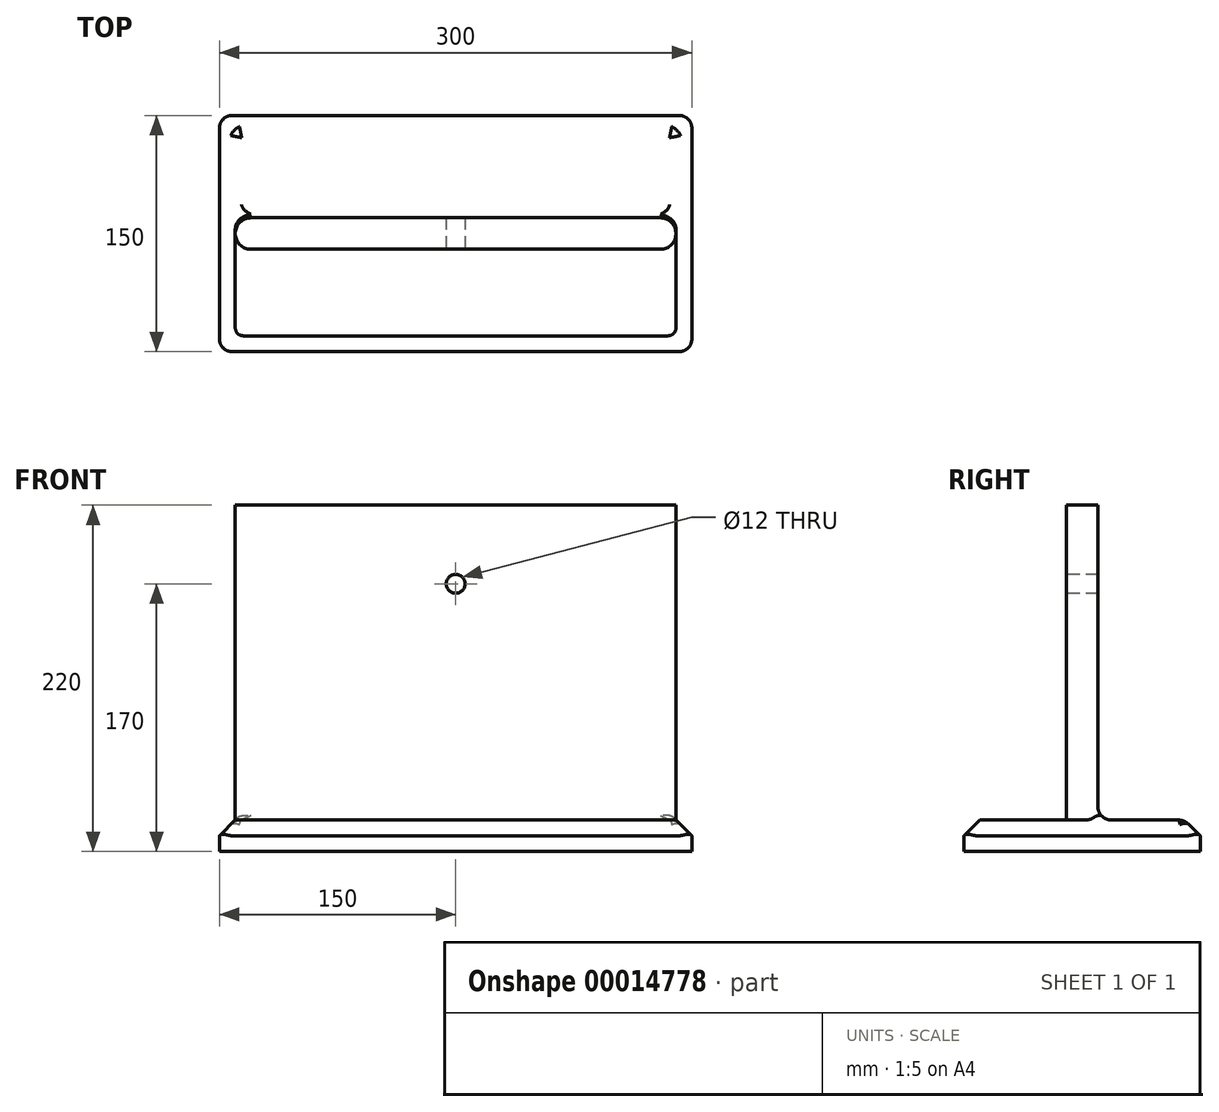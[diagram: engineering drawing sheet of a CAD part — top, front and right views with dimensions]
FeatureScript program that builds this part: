
annotation { "Feature Type Name" : "Feature", "Feature Type Description" : "" }
export const myFeature = defineFeature(function(context is Context, id is Id, definition is map)
    precondition{}
    {
        {
            var Q0;
            Q0=qCreatedBy(makeId("Top.planeOp"),FACE);
            var sketch = newSketch(context, id + "F0", { "sketchPlane" : qUnion([Q0])});
            skLineSegment(sketch, "E0.bottom", {"start": v(-150, 75) * mm, "end": v(150, 75) * mm});
            skLineSegment(sketch, "E0.top", {"start": v(-150, -75) * mm, "end": v(150, -75) * mm});
            skLineSegment(sketch, "E0.left", {"start": v(-150, 75) * mm, "end": v(-150, -75) * mm});
            skLineSegment(sketch, "E0.right", {"start": v(150, 75) * mm, "end": v(150, -75) * mm});
            skSolve(sketch);
        }
        {
            var Q0;
            Q0=makeQuery(id+"F0.imprint","IMPRINT",FACE,{"disambiguationData":[TD([[makeQuery(id+"F0.imprint","IMPRINT",EDGE,{"derivedFrom":sQuery(id+"F0.wireOp",EDGE,"E0.bottom")}),-1.0]])]});
            extrude(context, id + "F1", {"entities" : qUnion([Q0]), "depth" : 20 * mm});
        }
        {
            var Q0;
            Q0=makeQuery(id+"F1.opExtrude","CAP_EDGE",EDGE,{"disambiguationData":[OSD([sQuery(id+"F0.wireOp",EDGE,"E0.left")])],"isStart":false});
            var Q1;
            Q1=makeQuery(id+"F1.opExtrude","CAP_EDGE",EDGE,{"disambiguationData":[OSD([sQuery(id+"F0.wireOp",EDGE,"E0.bottom")])],"isStart":false});
            var Q2;
            Q2=makeQuery(id+"F1.opExtrude","CAP_EDGE",EDGE,{"disambiguationData":[OSD([sQuery(id+"F0.wireOp",EDGE,"E0.top")])],"isStart":false});
            var Q3;
            Q3=makeQuery(id+"F1.opExtrude","CAP_EDGE",EDGE,{"disambiguationData":[OSD([sQuery(id+"F0.wireOp",EDGE,"E0.right")])],"isStart":false});
            chamfer(context, id + "F2", {"entities" : qUnion([Q0, Q1, Q2, Q3]), "width" : 10 * mm, "tangentPropagation" : true});
        }
        {
            var Q0;
            Q0=makeQuery(id+"F1.opExtrude","SWEPT_EDGE",EDGE,{"disambiguationData":[OSD([sQuery(id+"F0.wireOp",EDGE,"E0.top"),sQuery(id+"F0.wireOp",EDGE,"E0.left")])]});
            var Q1;
            Q1=makeQuery(id+"F1.opExtrude","SWEPT_EDGE",EDGE,{"disambiguationData":[OSD([sQuery(id+"F0.wireOp",EDGE,"E0.bottom"),sQuery(id+"F0.wireOp",EDGE,"E0.left")])]});
            var Q2;
            Q2=makeQuery(id+"F2.opChamfer","BLEND_EDGE",EDGE,{"blendedFrom":[makeQuery(id+"F1.opExtrude","CAP_EDGE",EDGE,{"disambiguationData":[OSD([sQuery(id+"F0.wireOp",EDGE,"E0.bottom")])],"isStart":false}),makeQuery(id+"F1.opExtrude","CAP_EDGE",EDGE,{"disambiguationData":[OSD([sQuery(id+"F0.wireOp",EDGE,"E0.left")])],"isStart":false})],"blendedInto":[]});
            var Q3;
            Q3=makeQuery(id+"F2.opChamfer","BLEND_EDGE",EDGE,{"blendedFrom":[makeQuery(id+"F1.opExtrude","CAP_EDGE",EDGE,{"disambiguationData":[OSD([sQuery(id+"F0.wireOp",EDGE,"E0.top")])],"isStart":false}),makeQuery(id+"F1.opExtrude","CAP_EDGE",EDGE,{"disambiguationData":[OSD([sQuery(id+"F0.wireOp",EDGE,"E0.left")])],"isStart":false})],"blendedInto":[]});
            var Q4;
            Q4=makeQuery(id+"F2.opChamfer","BLEND_EDGE",EDGE,{"blendedFrom":[makeQuery(id+"F1.opExtrude","CAP_EDGE",EDGE,{"disambiguationData":[OSD([sQuery(id+"F0.wireOp",EDGE,"E0.top")])],"isStart":false}),makeQuery(id+"F1.opExtrude","CAP_EDGE",EDGE,{"disambiguationData":[OSD([sQuery(id+"F0.wireOp",EDGE,"E0.right")])],"isStart":false})],"blendedInto":[]});
            var Q5;
            Q5=makeQuery(id+"F1.opExtrude","SWEPT_EDGE",EDGE,{"disambiguationData":[OSD([sQuery(id+"F0.wireOp",EDGE,"E0.top"),sQuery(id+"F0.wireOp",EDGE,"E0.right")])]});
            var Q6;
            Q6=makeQuery(id+"F1.opExtrude","SWEPT_EDGE",EDGE,{"disambiguationData":[OSD([sQuery(id+"F0.wireOp",EDGE,"E0.bottom"),sQuery(id+"F0.wireOp",EDGE,"E0.right")])]});
            var Q7;
            Q7=makeQuery(id+"F2.opChamfer","BLEND_EDGE",EDGE,{"blendedFrom":[makeQuery(id+"F1.opExtrude","CAP_EDGE",EDGE,{"disambiguationData":[OSD([sQuery(id+"F0.wireOp",EDGE,"E0.bottom")])],"isStart":false}),makeQuery(id+"F1.opExtrude","CAP_EDGE",EDGE,{"disambiguationData":[OSD([sQuery(id+"F0.wireOp",EDGE,"E0.right")])],"isStart":false})],"blendedInto":[]});
            fillet(context, id + "F3", {"entities" : qUnion([Q0, Q1, Q2, Q3, Q4, Q5, Q6, Q7]), "radius" : 8 * mm, "tangentPropagation" : true, "allowEdgeOverflow" : false});
        }
        {
            var Q0;
            Q0=makeQuery(id+"F1.opExtrude","CAP_FACE",FACE,{"disambiguationData":[OSD([sQuery(id+"F0.wireOp",EDGE,"E0.bottom"),sQuery(id+"F0.wireOp",EDGE,"E0.top"),sQuery(id+"F0.wireOp",EDGE,"E0.left"),sQuery(id+"F0.wireOp",EDGE,"E0.right")])],"isStart":false});
            var sketch = newSketch(context, id + "F4", { "sketchPlane" : qUnion([Q0])});
            skLineSegment(sketch, "E1.bottom", {"start": v(-140, 10) * mm, "end": v(140, 10) * mm});
            skLineSegment(sketch, "E1.top", {"start": v(-140, -10) * mm, "end": v(140, -10) * mm});
            skLineSegment(sketch, "E1.left", {"start": v(-140, 10) * mm, "end": v(-140, -10) * mm});
            skLineSegment(sketch, "E1.right", {"start": v(140, 10) * mm, "end": v(140, -10) * mm});
            skSolve(sketch);
        }
        {
            var Q0;
            Q0=makeQuery(id+"F4.imprint","IMPRINT",FACE,{"disambiguationData":[TD([[makeQuery(id+"F4.imprint","IMPRINT",EDGE,{"derivedFrom":sQuery(id+"F4.wireOp",EDGE,"E1.bottom")}),-1.0]])]});
            extrude(context, id + "F5", {"entities" : qUnion([Q0]), "operationType" : NewBodyOperationType.ADD, "depth" : 200 * mm});
        }
        {
            var Q0;
            Q0=makeQuery(id+"F5.opExtrude","SWEPT_FACE",FACE,{"disambiguationData":[OSD([sQuery(id+"F4.wireOp",EDGE,"E1.top")])]});
            var sketch = newSketch(context, id + "F6", { "sketchPlane" : qUnion([Q0])});
            skCircle(sketch, "E2", {"center": v(0, 170) * mm, "radius": 6 * mm});
            skSolve(sketch);
        }
        {
            var Q0;
            Q0=makeQuery(id+"F6.imprint","IMPRINT",FACE,{"disambiguationData":[TD([[makeQuery(id+"F6.imprint","IMPRINT",EDGE,{"derivedFrom":sQuery(id+"F6.wireOp",EDGE,"E2")}),1.0]])]});
            var Q1;
            Q1=makeQuery(id+"F5.opExtrude","SWEPT_FACE",FACE,{"disambiguationData":[OSD([sQuery(id+"F4.wireOp",EDGE,"E1.bottom")])]});
            extrude(context, id + "F7", {"entities" : qUnion([Q0]), "operationType" : NewBodyOperationType.REMOVE, "endBound" : BoundingType.UP_TO_SURFACE, "oppositeDirection" : true, "endBoundEntityFace" : qUnion([Q1]), "depth" : 25 * mm});
        }
        {
            var Q0;
            Q0=makeQuery(id+"F5.opExtrude","CAP_EDGE",EDGE,{"disambiguationData":[OSD([sQuery(id+"F4.wireOp",EDGE,"E1.top")])],"isStart":true});
            var Q1;
            Q1=makeQuery(id+"F5.opExtrude","CAP_EDGE",EDGE,{"disambiguationData":[OSD([sQuery(id+"F4.wireOp",EDGE,"E1.bottom")])],"isStart":true});
            fillet(context, id + "F8", {"entities" : qUnion([Q0, Q1]), "radius" : 8.5 * mm, "tangentPropagation" : true, "allowEdgeOverflow" : false});
        }
        {
            var Q0;
            Q0=makeQuery(id+"F5.opExtrude","SWEPT_EDGE",EDGE,{"disambiguationData":[OSD([sQuery(id+"F0.wireOp",EDGE,"E0.bottom"),sQuery(id+"F0.wireOp",EDGE,"E0.top"),sQuery(id+"F0.wireOp",EDGE,"E0.left"),sQuery(id+"F0.wireOp",EDGE,"E0.right"),sQuery(id+"F4.wireOp",EDGE,"E1.top"),sQuery(id+"F4.wireOp",EDGE,"E1.right")])]});
            var Q1;
            Q1=makeQuery(id+"F5.opExtrude","SWEPT_EDGE",EDGE,{"disambiguationData":[OSD([sQuery(id+"F0.wireOp",EDGE,"E0.bottom"),sQuery(id+"F0.wireOp",EDGE,"E0.top"),sQuery(id+"F0.wireOp",EDGE,"E0.left"),sQuery(id+"F0.wireOp",EDGE,"E0.right"),sQuery(id+"F4.wireOp",EDGE,"E1.bottom"),sQuery(id+"F4.wireOp",EDGE,"E1.right")])]});
            var Q2;
            Q2=makeQuery(id+"F5.opExtrude","SWEPT_EDGE",EDGE,{"disambiguationData":[OSD([sQuery(id+"F0.wireOp",EDGE,"E0.bottom"),sQuery(id+"F0.wireOp",EDGE,"E0.top"),sQuery(id+"F0.wireOp",EDGE,"E0.left"),sQuery(id+"F0.wireOp",EDGE,"E0.right"),sQuery(id+"F4.wireOp",EDGE,"E1.bottom"),sQuery(id+"F4.wireOp",EDGE,"E1.left")])]});
            var Q3;
            Q3=makeQuery(id+"F5.opExtrude","SWEPT_EDGE",EDGE,{"disambiguationData":[OSD([sQuery(id+"F0.wireOp",EDGE,"E0.bottom"),sQuery(id+"F0.wireOp",EDGE,"E0.top"),sQuery(id+"F0.wireOp",EDGE,"E0.left"),sQuery(id+"F0.wireOp",EDGE,"E0.right"),sQuery(id+"F4.wireOp",EDGE,"E1.top"),sQuery(id+"F4.wireOp",EDGE,"E1.left")])]});
            fillet(context, id + "F9", {"entities" : qUnion([Q0, Q1, Q2, Q3]), "radius" : 10 * mm, "tangentPropagation" : true, "allowEdgeOverflow" : false});
        }
    });
